# Revit family: Practibox_S_cofrecito_empotrado_18_módulos_réf_137046_a_137259
name_source: partatom
category: Equipement électrique
revit_build: Autodesk Revit 2018 (Build: 20170223_1515(x64)
units: mm (PartAtom-declared; Revit-internal decimal feet)

## family parameters
Basée sur le plan de construction = Non
Configuration du panneau = Deux colonnes, circuits au sein
Cote de connecteur circulaire = Utiliser le diamètre
Couper avec des vides une fois chargée = Non
Numéro OmniClass = 23.80.30.11.17
Partagée = Non
Point de calcul de pièce = Non
Titre OmniClass = Distribution Boards and Control Panels
Toujours verticalement = Oui
Type d'élément = Tableau de raccordement

## types (32) — shared parameters
Condiciones Generales de Uso = https://export.legrand.com
Fabricant = "Legrand"
URL = www.legrand.com
anchura = 436 mm  [stored 1.43045 ft]

## per-type parameters (varying)
| type | 1R | 2R | 3R | 4R | Altura | Bornas N | Bornas T | Ina | profundidad | puerta B 1 r | puerta B 2 r | puerta B 3 r | puerta B 4 r | puerta T 1 r | puerta T 2 r | puerta T 3 r | puerta T 4 r | puerta blanca | puerta transparencia | tamaño |
| Practibox_S_cofrecito_empotrado_18_módulos_137066 | Oui | Non | Non | Non | 235 mm  [stored 0.770997 ft] |  | 13 salidas Icc 10kA | 63 A | 102 mm | Oui | Non | Non | Non | Non | Non | Non | Non | Oui | Non | 1 fila |
| Practibox_S_cofrecito_empotrado_18_módulos_137076 | Oui | Non | Non | Non | 235 mm  [stored 0.770997 ft] |  | 13 salidas Icc 10kA | 63 A | 102 mm | Non | Non | Non | Non | Oui | Non | Non | Non | Non | Oui | 1 fila |
| Practibox_S_cofrecito_empotrado_18_módulos_137246 | Oui | Non | Non | Non | 235 mm  [stored 0.770997 ft] | 13 salidas Icc 10kA | 13 salidas Icc 10kA | 63 A | 102 mm | Oui | Non | Non | Non | Non | Non | Non | Non | Oui | Non | 1 fila |
| Practibox_S_cofrecito_empotrado_18_módulos_137256 | Oui | Non | Non | Non | 235 mm  [stored 0.770997 ft] | 13 salidas Icc 10kA | 13 salidas Icc 10kA | 63 A | 102 mm | Non | Non | Non | Non | Oui | Non | Non | Non | Non | Oui | 1 fila |
| Practibox_S_cofrecito_empotrado_36_módulos_137067 | Non | Oui | Non | Non | 385 mm  [stored 1.26312 ft] |  | 22 salidas Icc 10kA | 90 A | 103 mm  [stored 0.337927 ft] | Non | Oui | Non | Non | Non | Non | Non | Non | Oui | Non | 2 fila |
| Practibox_S_cofrecito_empotrado_36_módulos_137077 | Non | Oui | Non | Non | 385 mm  [stored 1.26312 ft] |  | 22 salidas Icc 10kA | 90 A | 103 mm  [stored 0.337927 ft] | Non | Non | Non | Non | Non | Oui | Non | Non | Non | Oui | 2 fila |
| Practibox_S_cofrecito_empotrado_36_módulos_137257 | Non | Oui | Non | Non | 385 mm  [stored 1.26312 ft] | 22 salidas Icc 10kA | 22 salidas Icc 10kA | 90 A | 103 mm  [stored 0.337927 ft] | Non | Non | Non | Non | Non | Oui | Non | Non | Non | Oui | 2 fila |
| Practibox_S_cofrecito_empotrado_36_módulos_137247 | Non | Oui | Non | Non | 385 mm  [stored 1.26312 ft] | 22 salidas Icc 10kA | 22 salidas Icc 10kA | 90 A | 103 mm  [stored 0.337927 ft] | Non | Oui | Non | Non | Non | Non | Non | Non | Oui | Non | 2 fila |
| Practibox_S_cofrecito_empotrado_54_módulos_137078 | Non | Non | Oui | Non | 615 mm  [stored 2.01772 ft] |  | 35 salidas Icc 10kA | 90 A | 103 mm  [stored 0.337927 ft] | Non | Non | Non | Non | Non | Non | Oui | Non | Non | Oui | 3 fila |
| Practibox_S_cofrecito_empotrado_54_módulos_137068 | Non | Non | Oui | Non | 615 mm  [stored 2.01772 ft] |  | 35 salidas Icc 10kA | 90 A | 103 mm  [stored 0.337927 ft] | Non | Non | Oui | Non | Non | Non | Non | Non | Oui | Non | 3 fila |
| Practibox_S_cofrecito_empotrado_54_módulos_137248 | Non | Non | Oui | Non | 615 mm  [stored 2.01772 ft] | 35 salidas Icc 10kA | 35 salidas Icc 10kA | 90 A | 103 mm  [stored 0.337927 ft] | Non | Non | Oui | Non | Non | Non | Non | Non | Oui | Non | 3 fila |
| Practibox_S_cofrecito_empotrado_54_módulos_137258 | Non | Non | Oui | Non | 615 mm  [stored 2.01772 ft] | 35 salidas Icc 10kA | 35 salidas Icc 10kA | 90 A | 103 mm  [stored 0.337927 ft] | Non | Non | Non | Non | Non | Non | Oui | Non | Non | Oui | 3 fila |
| Practibox_S_cofrecito_empotrado_72_módulos_137079 | Non | Non | Non | Oui | 765 mm  [stored 2.50984 ft] |  | 35 salidas Icc 10kA | 90 A | 103 mm  [stored 0.337927 ft] | Non | Non | Non | Non | Non | Non | Non | Oui | Non | Oui | 4 fila |
| Practibox_S_cofrecito_empotrado_72_módulos_137069 | Non | Non | Non | Oui | 765 mm  [stored 2.50984 ft] |  | 35 salidas Icc 10kA | 90 A | 103 mm  [stored 0.337927 ft] | Non | Non | Non | Oui | Non | Non | Non | Non | Oui | Non | 4 fila |
| Practibox_S_cofrecito_empotrado_72_módulos_137259 | Non | Non | Non | Oui | 765 mm  [stored 2.50984 ft] | 35 salidas Icc 10kA | 35 salidas Icc 10kA | 90 A | 103 mm  [stored 0.337927 ft] | Non | Non | Non | Non | Non | Non | Non | Oui | Non | Oui | 4 fila |
| Practibox_S_cofrecito_empotrado_72_módulos_137249 | Non | Non | Non | Oui | 765 mm  [stored 2.50984 ft] | 35 salidas Icc 10kA | 35 salidas Icc 10kA | 90 A | 103 mm  [stored 0.337927 ft] | Non | Non | Non | Oui | Non | Non | Non | Non | Oui | Non | 4 fila |
| Practibox_S_cofrecito_empotrado_18_módulos_137056 | Oui | Non | Non | Non | 235 mm  [stored 0.770997 ft] |  | 13 salidas Icc 10kA | 63 A | 102 mm | Non | Non | Non | Non | Oui | Non | Non | Non | Non | Oui | 1 fila |
| Practibox_S_cofrecito_empotrado_18_módulos_137046 | Oui | Non | Non | Non | 235 mm  [stored 0.770997 ft] |  | 13 salidas Icc 10kA | 63 A | 102 mm | Oui | Non | Non | Non | Non | Non | Non | Non | Oui | Non | 1 fila |
| Practibox_S_cofrecito_empotrado_18_módulos_137226 | Oui | Non | Non | Non | 235 mm  [stored 0.770997 ft] | 13 salidas Icc 10kA | 13 salidas Icc 10kA | 63 A | 102 mm | Oui | Non | Non | Non | Non | Non | Non | Non | Oui | Non | 1 fila |
| Practibox_S_cofrecito_empotrado_18_módulos_137236 | Oui | Non | Non | Non | 235 mm  [stored 0.770997 ft] | 13 salidas Icc 10kA | 13 salidas Icc 10kA | 63 A | 102 mm | Non | Non | Non | Non | Oui | Non | Non | Non | Non | Oui | 1 fila |
| Practibox_S_cofrecito_empotrado_36_módulos_137237 | Non | Oui | Non | Non | 385 mm  [stored 1.26312 ft] | 22 salidas Icc 10kA | 22 salidas Icc 10kA | 90 A | 103 mm  [stored 0.337927 ft] | Non | Non | Non | Non | Non | Oui | Non | Non | Non | Oui | 2 fila |
| Practibox_S_cofrecito_empotrado_36_módulos_137057 | Non | Oui | Non | Non | 385 mm  [stored 1.26312 ft] |  | 22 salidas Icc 10kA | 90 A | 103 mm  [stored 0.337927 ft] | Non | Non | Non | Non | Non | Oui | Non | Non | Non | Oui | 2 fila |
| Practibox_S_cofrecito_empotrado_36_módulos_137047 | Non | Oui | Non | Non | 385 mm  [stored 1.26312 ft] |  | 22 salidas Icc 10kA | 90 A | 103 mm  [stored 0.337927 ft] | Non | Oui | Non | Non | Non | Non | Non | Non | Oui | Non | 2 fila |
| Practibox_S_cofrecito_empotrado_54_módulos_137238 | Non | Non | Oui | Non | 615 mm  [stored 2.01772 ft] | 35 salidas Icc 10kA | 35 salidas Icc 10kA | 90 A | 103 mm  [stored 0.337927 ft] | Non | Non | Non | Non | Non | Non | Oui | Non | Non | Oui | 3 fila |
| Practibox_S_cofrecito_empotrado_54_módulos_137228 | Non | Non | Oui | Non | 615 mm  [stored 2.01772 ft] | 35 salidas Icc 10kA | 35 salidas Icc 10kA | 90 A | 103 mm  [stored 0.337927 ft] | Non | Non | Oui | Non | Non | Non | Non | Non | Oui | Non | 3 fila |
| Practibox_S_cofrecito_empotrado_54_módulos_137048 | Non | Non | Oui | Non | 615 mm  [stored 2.01772 ft] |  | 35 salidas Icc 10kA | 90 A | 103 mm  [stored 0.337927 ft] | Non | Non | Oui | Non | Non | Non | Non | Non | Oui | Non | 3 fila |
| Practibox_S_cofrecito_empotrado_54_módulos_137058 | Non | Non | Oui | Non | 615 mm  [stored 2.01772 ft] |  | 35 salidas Icc 10kA | 90 A | 103 mm  [stored 0.337927 ft] | Non | Non | Non | Non | Non | Non | Oui | Non | Non | Oui | 3 fila |
| Practibox_S_cofrecito_empotrado_72_módulos_137239 | Non | Non | Non | Oui | 765 mm  [stored 2.50984 ft] | 35 salidas Icc 10kA | 35 salidas Icc 10kA | 90 A | 103 mm  [stored 0.337927 ft] | Non | Non | Non | Non | Non | Non | Non | Oui | Non | Oui | 4 fila |
| Practibox_S_cofrecito_empotrado_72_módulos_137229 | Non | Non | Non | Oui | 765 mm  [stored 2.50984 ft] | 35 salidas Icc 10kA | 35 salidas Icc 10kA | 90 A | 103 mm  [stored 0.337927 ft] | Non | Non | Non | Oui | Non | Non | Non | Non | Oui | Non | 4 fila |
| Practibox_S_cofrecito_empotrado_72_módulos_137049 | Non | Non | Non | Oui | 765 mm  [stored 2.50984 ft] |  | 35 salidas Icc 10kA | 90 A | 103 mm  [stored 0.337927 ft] | Non | Non | Non | Oui | Non | Non | Non | Non | Oui | Non | 4 fila |
| Practibox_S_cofrecito_empotrado_72_módulos_137059 | Non | Non | Non | Oui | 765 mm  [stored 2.50984 ft] |  | 35 salidas Icc 10kA | 90 A | 103 mm  [stored 0.337927 ft] | Non | Non | Non | Non | Non | Non | Non | Oui | Non | Oui | 4 fila |
| Practibox_S_cofrecito_empotrado_36_módulos_137227 | Non | Oui | Non | Non | 385 mm  [stored 1.26312 ft] | 22 salidas Icc 10kA | 22 salidas Icc 10kA | 90 A | 103 mm  [stored 0.337927 ft] | Non | Oui | Non | Non | Non | Non | Non | Non | Oui | Non | 2 fila |

note: column(s) folded — value = type name in every type: Description

note: [stored X ft] marks values corroborated as IEEE doubles in the binary element streams (Revit-internal decimal feet)
